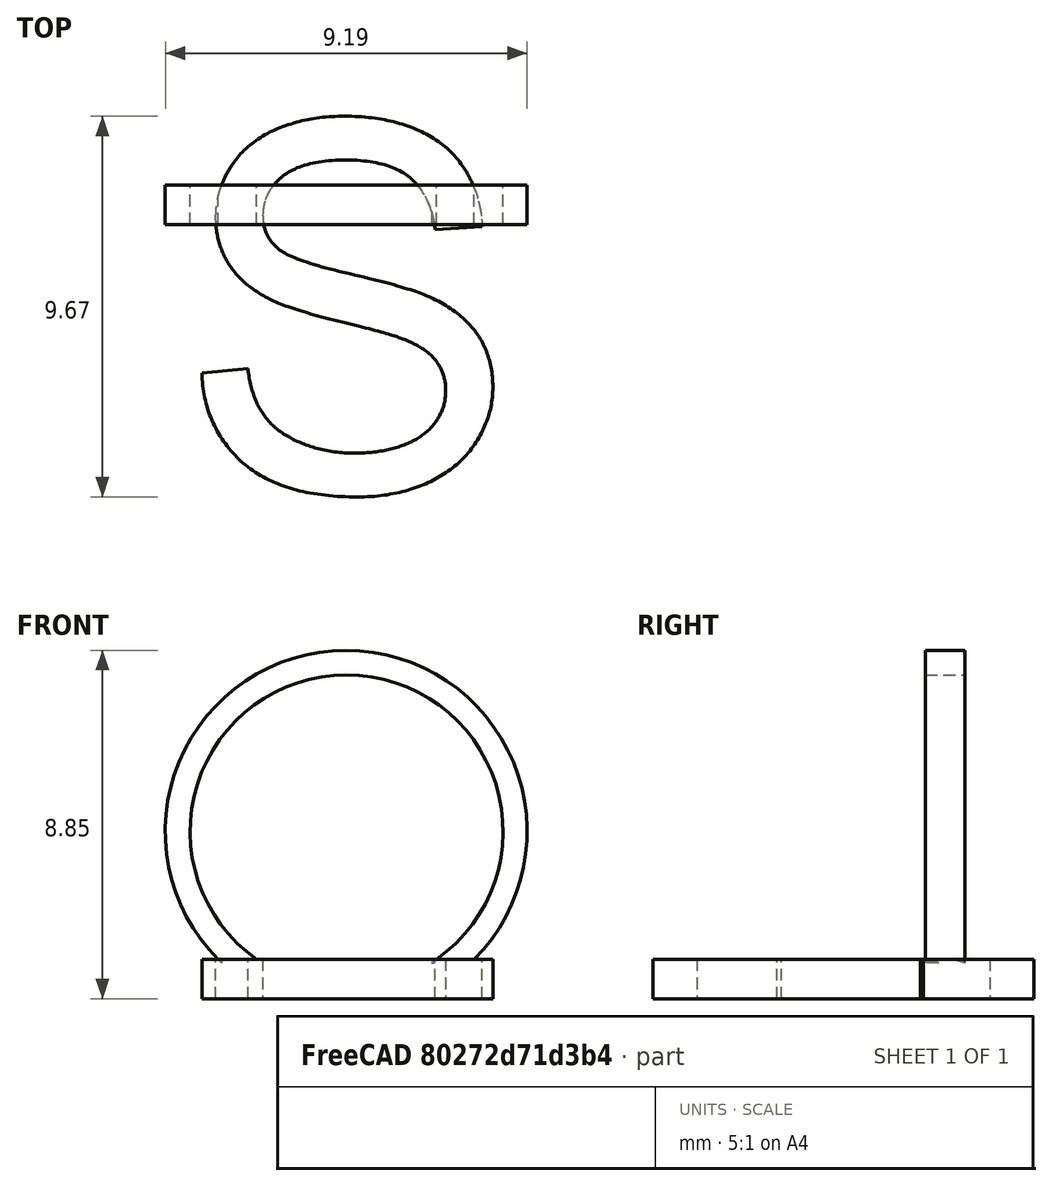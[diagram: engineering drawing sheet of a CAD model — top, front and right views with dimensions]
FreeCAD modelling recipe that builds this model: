
FCSTD DOCUMENT  (FreeCAD 0.21R33668 +26 (Git))
Label: URing
License: All rights reserved
LicenseURL: https://en.wikipedia.org/wiki/All_rights_reserved
objects: PartDesign::Body×2, PartDesign::Pad×2, Part::Part2DObjectPython×1, Sketcher::SketchObject×1, Part::Fuse×1
note: 9 computed .brp shape members not serialized (recipe doc carries the construction recipe); baked Part::Feature solids carry a one-line shape summary decoded from their .brp

FEATURE [Part::Part2DObjectPython] ShapeString  # Draft 2D object (typed FeaturePython)
  FontFile = <path>
  MakeFace = true
  Placement = pos=(-5.83,-7.66,0) rot=(0,0,1.0001;1e-06rad)
  Size = 10
  String = S
  Tracking = 0
FEATURE [PartDesign::Body] Body
  Group = -> [ShapeString]
  Origin = -> Origin
FEATURE [PartDesign::Pad] Pad001
  Direction = (-2.36e-13,2.2e-14,1)
  Length = 1
  Length2 = 10
  Placement = pos=(-5.83,-7.66,0) rot=(0,0,1.0001;1e-06rad)
  Profile = -> ShapeString
  ReferenceAxis = -> ShapeString [N_Axis]
  Type = 0
FEATURE [Sketcher::SketchObject] Sketch
  FullyConstrained = false
  Placement = pos=(0,0,0) rot=(1,0,0;1.5708rad)
  sketch-geometry (4):
    g0: ArcOfCircle CenterX=-1.45563 CenterY=4.25116 CenterZ=0 NormalX=0 NormalY=0 NormalZ=1 AngleXU=0 Radius=3.97606 StartAngle=5.28555 EndAngle=10.4237
    g1: ArcOfCircle CenterX=-1.46662 CenterY=4.25073 CenterZ=0 NormalX=0 NormalY=0 NormalZ=1 AngleXU=0 Radius=4.59705 StartAngle=5.46982 EndAngle=10.239
    g2: LineSegment StartX=-4.62217 StartY=0.907763 StartZ=0 EndX=-3.60754 EndY=0.907763 EndZ=0
    g3: LineSegment StartX=0.700535 StartY=0.910504 StartZ=0 EndX=1.69183 EndY=0.910504 EndZ=0
  constraints (6):
    c: Horizontal(g2)
    c: Horizontal(g3)
    c: Coincident(g1,g2)
    c: Coincident(g1,g3)
    c: Coincident(g0,g2)
    c: Coincident(g0,g3)
FEATURE [PartDesign::Pad] Pad
  Direction = (0,-1,2e-16)
  Length = 1
  Length2 = 10
  Placement = pos=(0,0,0) rot=(1,0,0;1.5708rad)
  Profile = -> Sketch
  ReferenceAxis = -> Sketch [N_Axis]
  Type = 0
FEATURE [PartDesign::Body] Body002
  Group = -> [Sketch,Pad]
  Origin = -> Origin002
  Placement = pos=(-0.1,0.1,0) rot=(0,0,1;0rad)
  Tip = -> Pad
FEATURE [Part::Fuse] Fusion
  Base = -> Pad001
  Tool = -> Body002
note: 1 file-system path scrubbed to <path> (originals preserved in the JSON sidecar)
